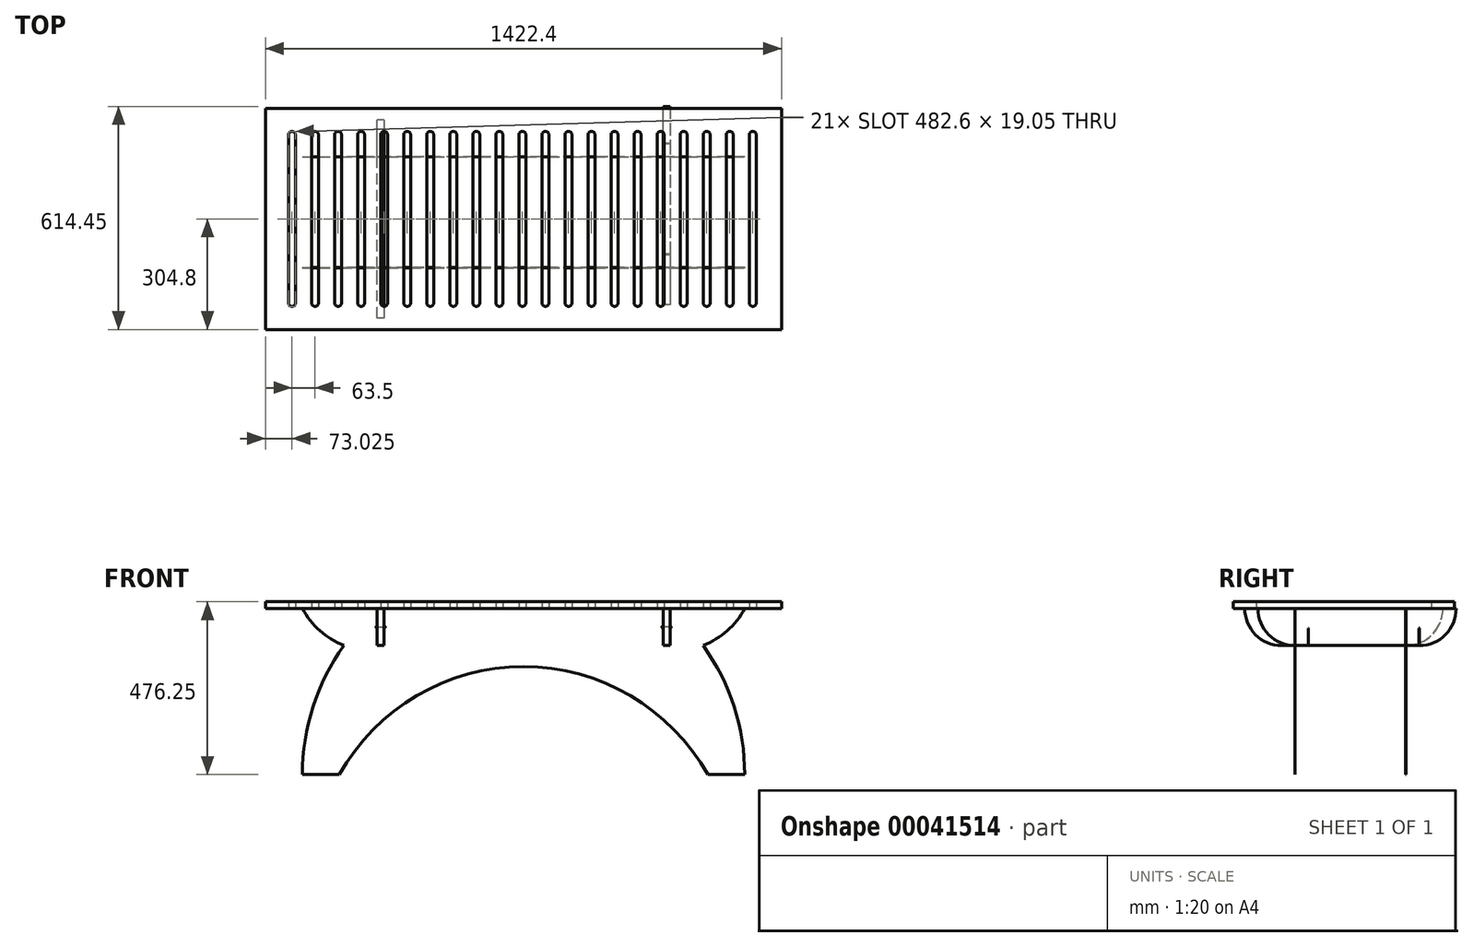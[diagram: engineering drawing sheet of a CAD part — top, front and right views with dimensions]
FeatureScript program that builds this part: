
annotation { "Feature Type Name" : "Feature", "Feature Type Description" : "" }
export const myFeature = defineFeature(function(context is Context, id is Id, definition is map)
    precondition{}
    {
        {
            assignVariable(context, id + "F0", {"name" : "Thickness", "anyValue" : .75});
        }
        {
            var Q0;
            Q0=qCreatedBy(makeId("Front.planeOp"),FACE);
            var sketch = newSketch(context, id + "F1", { "sketchPlane" : qUnion([Q0])});
            skLineSegment(sketch, "E0.bottom", {"start": v(-305.21, 223.52) * mm, "end": v(-99.17, 223.52) * mm});
            skLineSegment(sketch, "E0.top", {"start": v(-305.21, -233.68) * mm, "end": v(-203.61, -233.68) * mm});
            skLineSegment(sketch, "E1", {"start": v(913.99, -233.68) * mm, "end": v(812.39, -233.68) * mm});
            skArc(sketch, "E2", {"start": v(812.39, -233.68) * mm, "mid": v(304.39, 63.53) * mm, "end": v(-203.61, -233.68) * mm});
            skArc(sketch, "E3", {"start": v(913.99, -233.68) * mm, "mid": v(884.67, -46.9) * mm, "end": v(799.53, 121.92) * mm});
            skArc(sketch, "E4.trimOffspring", {"start": v(-190.75, 121.92) * mm, "mid": v(-275.89, -46.9) * mm, "end": v(-305.21, -233.68) * mm});
            skArc(sketch, "E5", {"start": v(-305.21, 223.52) * mm, "mid": v(-256.98, 162.58) * mm, "end": v(-190.75, 121.92) * mm});
            skArc(sketch, "E6", {"start": v(799.53, 121.92) * mm, "mid": v(865.76, 162.58) * mm, "end": v(913.99, 223.52) * mm});
            skLineSegment(sketch, "E7.trimOffspring", {"start": v(812.39, -233.68) * mm, "end": v(913.99, -233.68) * mm});
            skLineSegment(sketch, "E8", {"start": v(-99.17, 223.52) * mm, "end": v(-99.17, 175.9) * mm});
            skLineSegment(sketch, "E9", {"start": v(-96, 172.72) * mm, "end": v(-83.3, 172.72) * mm});
            skLineSegment(sketch, "E10", {"start": v(-80.12, 175.9) * mm, "end": v(-80.12, 223.52) * mm});
            skLineSegment(sketch, "E11", {"start": v(304.39, 63.53) * mm, "end": v(304.39, 223.52) * mm, "construction": true});
            skLineSegment(sketch, "E12.MirrorCS", {"start": v(707.95, 223.52) * mm, "end": v(707.95, 175.9) * mm});
            skLineSegment(sketch, "E13.MirrorCS", {"start": v(688.9, 175.9) * mm, "end": v(688.9, 223.52) * mm});
            skLineSegment(sketch, "E14.MirrorCS", {"start": v(704.78, 172.72) * mm, "end": v(692.08, 172.72) * mm});
            skLineSegment(sketch, "E15.trimOffspring", {"start": v(-80.12, 223.52) * mm, "end": v(688.9, 223.52) * mm});
            skLineSegment(sketch, "E16.trimOffspring", {"start": v(707.95, 223.52) * mm, "end": v(913.99, 223.52) * mm});
            skArc(sketch, "E17", {"start": v(-99.17, 175.9) * mm, "mid": v(-101.42, 170.48) * mm, "end": v(-96, 172.72) * mm});
            skArc(sketch, "E18", {"start": v(-83.3, 172.72) * mm, "mid": v(-77.88, 170.48) * mm, "end": v(-80.12, 175.9) * mm});
            skArc(sketch, "E19", {"start": v(688.9, 175.9) * mm, "mid": v(686.66, 170.48) * mm, "end": v(692.08, 172.72) * mm});
            skArc(sketch, "E20", {"start": v(704.78, 172.72) * mm, "mid": v(710.2, 170.48) * mm, "end": v(707.95, 175.9) * mm});
            skSolve(sketch);
        }
        {
            var Q0;
            Q0=qSketchRegion(id+"F1",true);
            extrude(context, id + "F2", {"entities" : qUnion([Q0]), "depth" : (getVariable(context, 'Thickness')) * mm});
        }
        {
            var Q0;
            Q0=makeQuery(id+"F2.opExtrude","CAP_FACE",FACE,{"disambiguationData":[OSD([sQuery(id+"F1.wireOp",EDGE,"E0.bottom"),sQuery(id+"F1.wireOp",EDGE,"E0.top"),sQuery(id+"F1.wireOp",EDGE,"E2"),sQuery(id+"F1.wireOp",EDGE,"E3"),sQuery(id+"F1.wireOp",EDGE,"E4.trimOffspring"),sQuery(id+"F1.wireOp",EDGE,"E5"),sQuery(id+"F1.wireOp",EDGE,"E6"),sQuery(id+"F1.wireOp",EDGE,"E7.trimOffspring"),sQuery(id+"F1.wireOp",EDGE,"E8"),sQuery(id+"F1.wireOp",EDGE,"E9"),sQuery(id+"F1.wireOp",EDGE,"E10"),sQuery(id+"F1.wireOp",EDGE,"E12.MirrorCS"),sQuery(id+"F1.wireOp",EDGE,"E13.MirrorCS"),sQuery(id+"F1.wireOp",EDGE,"E14.MirrorCS"),sQuery(id+"F1.wireOp",EDGE,"E15.trimOffspring"),sQuery(id+"F1.wireOp",EDGE,"E16.trimOffspring")])],"isStart":false});
            cPlane(context, id + "F3", {"entities" : qUnion([Q0]), "cplaneType" : CPlaneType.OFFSET, "offset" : 152.4 * mm, "width" : 152.4 * mm, "height" : 152.4 * mm});
        }
        {
            var Q0;
            Q0=makeQuery(id+"F2.opExtrude","SWEPT_BODY",BODY,{"disambiguationData":[OSD([sQuery(id+"F1.wireOp",EDGE,"E0.bottom"),sQuery(id+"F1.wireOp",EDGE,"E0.top"),sQuery(id+"F1.wireOp",EDGE,"E2"),sQuery(id+"F1.wireOp",EDGE,"E3"),sQuery(id+"F1.wireOp",EDGE,"E4.trimOffspring"),sQuery(id+"F1.wireOp",EDGE,"E5"),sQuery(id+"F1.wireOp",EDGE,"E6"),sQuery(id+"F1.wireOp",EDGE,"E7.trimOffspring"),sQuery(id+"F1.wireOp",EDGE,"E8"),sQuery(id+"F1.wireOp",EDGE,"E9"),sQuery(id+"F1.wireOp",EDGE,"E10"),sQuery(id+"F1.wireOp",EDGE,"E12.MirrorCS"),sQuery(id+"F1.wireOp",EDGE,"E13.MirrorCS"),sQuery(id+"F1.wireOp",EDGE,"E14.MirrorCS"),sQuery(id+"F1.wireOp",EDGE,"E15.trimOffspring"),sQuery(id+"F1.wireOp",EDGE,"E16.trimOffspring")])]});
            var Q1;
            Q1=qCreatedBy(id+"F3.planeOp",FACE);
            mirror(context, id + "F4", {"entities" : qUnion([Q0]), "mirrorPlane" : qUnion([Q1])});
        }
        {
            var Q0;
            Q0=makeQuery(id+"F4.opPattern","COPY",FACE,{"derivedFrom":makeQuery(id+"F2.opExtrude","SWEPT_FACE",FACE,{"disambiguationData":[OSD([sQuery(id+"F1.wireOp",EDGE,"E8")])]}),"instanceName":"1"});
            var sketch = newSketch(context, id + "F5", { "sketchPlane" : qUnion([Q0])});
            skLineSegment(sketch, "E21.bottom", {"start": v(-444.5, 223.52) * mm, "end": v(101.6, 223.52) * mm});
            skLineSegment(sketch, "E21.top", {"start": v(-342.9, 121.92) * mm, "end": v(0, 121.92) * mm});
            skArc(sketch, "E22", {"start": v(-444.5, 223.52) * mm, "mid": v(-414.74, 151.68) * mm, "end": v(-342.9, 121.92) * mm});
            skArc(sketch, "E23.converted", {"start": v(0, 121.92) * mm, "mid": v(71.84, 151.68) * mm, "end": v(101.6, 223.52) * mm});
            skSolve(sketch);
        }
        {
            var Q0;
            Q0=qSketchRegion(id+"F5",true);
            var Q1;
            Q1=makeQuery(id+"F2.opExtrude","SWEPT_FACE",FACE,{"disambiguationData":[OSD([sQuery(id+"F1.wireOp",EDGE,"E10")])]});
            extrude(context, id + "F6", {"entities" : qUnion([Q0]), "endBound" : BoundingType.UP_TO_SURFACE, "endBoundEntityFace" : qUnion([Q1]), "depth" : 25.4 * mm});
        }
        {
            var Q0;
            Q0=makeQuery(id+"F2.opExtrude","SWEPT_BODY",BODY,{"disambiguationData":[OSD([sQuery(id+"F1.wireOp",EDGE,"E0.bottom"),sQuery(id+"F1.wireOp",EDGE,"E0.top"),sQuery(id+"F1.wireOp",EDGE,"E2"),sQuery(id+"F1.wireOp",EDGE,"E3"),sQuery(id+"F1.wireOp",EDGE,"E4.trimOffspring"),sQuery(id+"F1.wireOp",EDGE,"E5"),sQuery(id+"F1.wireOp",EDGE,"E6"),sQuery(id+"F1.wireOp",EDGE,"E7.trimOffspring"),sQuery(id+"F1.wireOp",EDGE,"E8"),sQuery(id+"F1.wireOp",EDGE,"E9"),sQuery(id+"F1.wireOp",EDGE,"E10"),sQuery(id+"F1.wireOp",EDGE,"E12.MirrorCS"),sQuery(id+"F1.wireOp",EDGE,"E13.MirrorCS"),sQuery(id+"F1.wireOp",EDGE,"E14.MirrorCS"),sQuery(id+"F1.wireOp",EDGE,"E15.trimOffspring"),sQuery(id+"F1.wireOp",EDGE,"E16.trimOffspring")])]});
            var Q1;
            Q1=makeQuery(id+"F4.opPattern","COPY",BODY,{"derivedFrom":makeQuery(id+"F2.opExtrude","SWEPT_BODY",BODY,{"disambiguationData":[OSD([sQuery(id+"F1.wireOp",EDGE,"E0.bottom"),sQuery(id+"F1.wireOp",EDGE,"E0.top"),sQuery(id+"F1.wireOp",EDGE,"E2"),sQuery(id+"F1.wireOp",EDGE,"E3"),sQuery(id+"F1.wireOp",EDGE,"E4.trimOffspring"),sQuery(id+"F1.wireOp",EDGE,"E5"),sQuery(id+"F1.wireOp",EDGE,"E6"),sQuery(id+"F1.wireOp",EDGE,"E7.trimOffspring"),sQuery(id+"F1.wireOp",EDGE,"E8"),sQuery(id+"F1.wireOp",EDGE,"E9"),sQuery(id+"F1.wireOp",EDGE,"E10"),sQuery(id+"F1.wireOp",EDGE,"E12.MirrorCS"),sQuery(id+"F1.wireOp",EDGE,"E13.MirrorCS"),sQuery(id+"F1.wireOp",EDGE,"E14.MirrorCS"),sQuery(id+"F1.wireOp",EDGE,"E15.trimOffspring"),sQuery(id+"F1.wireOp",EDGE,"E16.trimOffspring")])]}),"instanceName":"1"});
            var Q2;
            Q2=makeQuery(id+"F6.opExtrude","SWEPT_BODY",BODY,{"disambiguationData":[OSD([sQuery(id+"F5.wireOp",EDGE,"E21.bottom"),sQuery(id+"F5.wireOp",EDGE,"E21.top"),sQuery(id+"F5.wireOp",EDGE,"E22"),sQuery(id+"F5.wireOp",EDGE,"E23.converted")])]});
            booleanBodies(context, id + "F7", {"operationType" : BooleanOperationType.SUBTRACTION, "tools" : qUnion([Q0, Q1]), "targets" : qUnion([Q2]), "keepTools" : true});
        }
        {
            var Q0;
            Q0=makeQuery(id+"F2.opExtrude","SWEPT_FACE",FACE,{"disambiguationData":[OSD([sQuery(id+"F1.wireOp",EDGE,"E12.MirrorCS")])]});
            var Q1;
            Q1=makeQuery(id+"F6.opExtrude","CAP_FACE",FACE,{"disambiguationData":[OSD([sQuery(id+"F5.wireOp",EDGE,"E21.bottom"),sQuery(id+"F5.wireOp",EDGE,"E21.top"),sQuery(id+"F5.wireOp",EDGE,"E22"),sQuery(id+"F5.wireOp",EDGE,"E23.converted")])],"isStart":true});
            cPlane(context, id + "F8", {"entities" : qUnion([Q0, Q1]), "cplaneType" : CPlaneType.MID_PLANE, "offset" : 152.4 * mm, "width" : 152.4 * mm, "height" : 152.4 * mm});
        }
        {
            var Q0;
            Q0=makeQuery(id+"F6.opExtrude","SWEPT_BODY",BODY,{"disambiguationData":[OSD([sQuery(id+"F5.wireOp",EDGE,"E21.bottom"),sQuery(id+"F5.wireOp",EDGE,"E21.top"),sQuery(id+"F5.wireOp",EDGE,"E22"),sQuery(id+"F5.wireOp",EDGE,"E23.converted")])]});
            var Q1;
            Q1=sQuery(id+"F5.wireOp",VERTEX,"E22.center");
            var Q2;
            Q2=makeQuery(id+"F4.opPattern","COPY",VERTEX,{"derivedFrom":makeQuery(id+"F2.opExtrude","CAP_VERTEX",VERTEX,{"disambiguationData":[OSD([sQuery(id+"F1.wireOp",EDGE,"E13.MirrorCS"),sQuery(id+"F1.wireOp",EDGE,"E15.trimOffspring")])],"isStart":true}),"instanceName":"1"});
            transform(context, id + "F9", {"entities" : qUnion([Q0]), "transformType" : TransformType.TRANSLATION_ENTITY, "oppositeDirectionEntity" : false, "transformLine" : qUnion([Q1, Q2]), "makeCopy" : true});
        }
        {
            var Q0;
            Q0=qCreatedBy(makeId("Top.planeOp"),FACE);
            var sketch = newSketch(context, id + "F10", { "sketchPlane" : qUnion([Q0])});
            skLineSegment(sketch, "E24.bottom", {"start": v(-252.18, 107.3) * mm, "end": v(1170.22, 107.3) * mm});
            skLineSegment(sketch, "E24.top", {"start": v(-252.18, -502.3) * mm, "end": v(1170.22, -502.3) * mm});
            skLineSegment(sketch, "E24.left", {"start": v(-252.18, 107.3) * mm, "end": v(-252.18, -502.3) * mm});
            skLineSegment(sketch, "E24.right", {"start": v(1170.22, 107.3) * mm, "end": v(1170.22, -502.3) * mm});
            skLineSegment(sketch, "E25.bottom", {"start": v(-179.15, 43.8) * mm, "end": v(-179.15, 43.8) * mm});
            skLineSegment(sketch, "E25.top", {"start": v(-179.15, -438.8) * mm, "end": v(-179.15, -438.8) * mm});
            skLineSegment(sketch, "E25.left", {"start": v(-188.68, 34.27) * mm, "end": v(-188.68, -429.28) * mm});
            skLineSegment(sketch, "E25.right", {"start": v(-169.63, 34.27) * mm, "end": v(-169.63, -429.28) * mm});
            skPoint(sketch, "E26.visualSharp", {"position": v(-188.68, 43.8) * mm});
            skArc(sketch, "E26.filletArc", {"start": v(-179.15, 43.8) * mm, "mid": v(-185.89, 41) * mm, "end": v(-188.68, 34.27) * mm});
            skPoint(sketch, "E27.visualSharp", {"position": v(-169.63, 43.8) * mm});
            skArc(sketch, "E27.filletArc", {"start": v(-169.63, 34.27) * mm, "mid": v(-172.42, 41) * mm, "end": v(-179.15, 43.8) * mm});
            skPoint(sketch, "E28.visualSharp", {"position": v(-188.68, -438.8) * mm});
            skArc(sketch, "E28.filletArc", {"start": v(-188.68, -429.28) * mm, "mid": v(-185.89, -436.01) * mm, "end": v(-179.15, -438.8) * mm});
            skPoint(sketch, "E29.visualSharp", {"position": v(-169.63, -438.8) * mm});
            skArc(sketch, "E29.filletArc", {"start": v(-179.15, -438.8) * mm, "mid": v(-172.42, -436.01) * mm, "end": v(-169.63, -429.28) * mm});
            skArc(sketch, "E30.1.0.0", {"start": v(-115.65, 43.8) * mm, "mid": v(-122.39, 41) * mm, "end": v(-125.18, 34.27) * mm});
            skArc(sketch, "E30.1.0.1", {"start": v(-106.13, 34.27) * mm, "mid": v(-108.92, 41) * mm, "end": v(-115.65, 43.8) * mm});
            skLineSegment(sketch, "E30.1.0.2", {"start": v(-106.13, 34.27) * mm, "end": v(-106.13, -429.28) * mm});
            skLineSegment(sketch, "E30.1.0.3", {"start": v(-125.18, 34.27) * mm, "end": v(-125.18, -429.28) * mm});
            skArc(sketch, "E30.1.0.4", {"start": v(-125.18, -429.28) * mm, "mid": v(-122.39, -436.01) * mm, "end": v(-115.65, -438.8) * mm});
            skArc(sketch, "E30.1.0.5", {"start": v(-115.65, -438.8) * mm, "mid": v(-108.92, -436.01) * mm, "end": v(-106.13, -429.28) * mm});
            skArc(sketch, "E30.2.0.0", {"start": v(-52.15, 43.8) * mm, "mid": v(-58.89, 41) * mm, "end": v(-61.68, 34.27) * mm});
            skArc(sketch, "E30.2.0.1", {"start": v(-42.63, 34.27) * mm, "mid": v(-45.42, 41) * mm, "end": v(-52.15, 43.8) * mm});
            skLineSegment(sketch, "E30.2.0.2", {"start": v(-42.63, 34.27) * mm, "end": v(-42.63, -429.28) * mm});
            skLineSegment(sketch, "E30.2.0.3", {"start": v(-61.68, 34.27) * mm, "end": v(-61.68, -429.28) * mm});
            skArc(sketch, "E30.2.0.4", {"start": v(-61.68, -429.28) * mm, "mid": v(-58.89, -436.01) * mm, "end": v(-52.15, -438.8) * mm});
            skArc(sketch, "E30.2.0.5", {"start": v(-52.15, -438.8) * mm, "mid": v(-45.42, -436.01) * mm, "end": v(-42.63, -429.28) * mm});
            skArc(sketch, "E30.3.0.0", {"start": v(11.35, 43.8) * mm, "mid": v(4.61, 41) * mm, "end": v(1.82, 34.27) * mm});
            skArc(sketch, "E30.3.0.1", {"start": v(20.87, 34.27) * mm, "mid": v(18.08, 41) * mm, "end": v(11.35, 43.8) * mm});
            skLineSegment(sketch, "E30.3.0.2", {"start": v(20.87, 34.27) * mm, "end": v(20.87, -429.28) * mm});
            skLineSegment(sketch, "E30.3.0.3", {"start": v(1.82, 34.27) * mm, "end": v(1.82, -429.28) * mm});
            skArc(sketch, "E30.3.0.4", {"start": v(1.82, -429.28) * mm, "mid": v(4.61, -436.01) * mm, "end": v(11.35, -438.8) * mm});
            skArc(sketch, "E30.3.0.5", {"start": v(11.35, -438.8) * mm, "mid": v(18.08, -436.01) * mm, "end": v(20.87, -429.28) * mm});
            skArc(sketch, "E30.4.0.0", {"start": v(74.85, 43.8) * mm, "mid": v(68.11, 41) * mm, "end": v(65.32, 34.27) * mm});
            skArc(sketch, "E30.4.0.1", {"start": v(84.37, 34.27) * mm, "mid": v(81.58, 41) * mm, "end": v(74.85, 43.8) * mm});
            skLineSegment(sketch, "E30.4.0.2", {"start": v(84.37, 34.27) * mm, "end": v(84.37, -429.28) * mm});
            skLineSegment(sketch, "E30.4.0.3", {"start": v(65.32, 34.27) * mm, "end": v(65.32, -429.28) * mm});
            skArc(sketch, "E30.4.0.4", {"start": v(65.32, -429.28) * mm, "mid": v(68.11, -436.01) * mm, "end": v(74.85, -438.8) * mm});
            skArc(sketch, "E30.4.0.5", {"start": v(74.85, -438.8) * mm, "mid": v(81.58, -436.01) * mm, "end": v(84.37, -429.28) * mm});
            skArc(sketch, "E30.5.0.0", {"start": v(138.35, 43.8) * mm, "mid": v(131.61, 41) * mm, "end": v(128.82, 34.27) * mm});
            skArc(sketch, "E30.5.0.1", {"start": v(147.87, 34.27) * mm, "mid": v(145.08, 41) * mm, "end": v(138.35, 43.8) * mm});
            skLineSegment(sketch, "E30.5.0.2", {"start": v(147.87, 34.27) * mm, "end": v(147.87, -429.28) * mm});
            skLineSegment(sketch, "E30.5.0.3", {"start": v(128.82, 34.27) * mm, "end": v(128.82, -429.28) * mm});
            skArc(sketch, "E30.5.0.4", {"start": v(128.82, -429.28) * mm, "mid": v(131.61, -436.01) * mm, "end": v(138.35, -438.8) * mm});
            skArc(sketch, "E30.5.0.5", {"start": v(138.35, -438.8) * mm, "mid": v(145.08, -436.01) * mm, "end": v(147.87, -429.28) * mm});
            skArc(sketch, "E30.6.0.0", {"start": v(201.85, 43.8) * mm, "mid": v(195.11, 41) * mm, "end": v(192.32, 34.27) * mm});
            skArc(sketch, "E30.6.0.1", {"start": v(211.37, 34.27) * mm, "mid": v(208.58, 41) * mm, "end": v(201.85, 43.8) * mm});
            skLineSegment(sketch, "E30.6.0.2", {"start": v(211.37, 34.27) * mm, "end": v(211.37, -429.28) * mm});
            skLineSegment(sketch, "E30.6.0.3", {"start": v(192.32, 34.27) * mm, "end": v(192.32, -429.28) * mm});
            skArc(sketch, "E30.6.0.4", {"start": v(192.32, -429.28) * mm, "mid": v(195.11, -436.01) * mm, "end": v(201.85, -438.8) * mm});
            skArc(sketch, "E30.6.0.5", {"start": v(201.85, -438.8) * mm, "mid": v(208.58, -436.01) * mm, "end": v(211.37, -429.28) * mm});
            skArc(sketch, "E30.7.0.0", {"start": v(265.35, 43.8) * mm, "mid": v(258.61, 41) * mm, "end": v(255.82, 34.27) * mm});
            skArc(sketch, "E30.7.0.1", {"start": v(274.87, 34.27) * mm, "mid": v(272.08, 41) * mm, "end": v(265.35, 43.8) * mm});
            skLineSegment(sketch, "E30.7.0.2", {"start": v(274.87, 34.27) * mm, "end": v(274.87, -429.28) * mm});
            skLineSegment(sketch, "E30.7.0.3", {"start": v(255.82, 34.27) * mm, "end": v(255.82, -429.28) * mm});
            skArc(sketch, "E30.7.0.4", {"start": v(255.82, -429.28) * mm, "mid": v(258.61, -436.01) * mm, "end": v(265.35, -438.8) * mm});
            skArc(sketch, "E30.7.0.5", {"start": v(265.35, -438.8) * mm, "mid": v(272.08, -436.01) * mm, "end": v(274.87, -429.28) * mm});
            skArc(sketch, "E30.8.0.0", {"start": v(328.85, 43.8) * mm, "mid": v(322.11, 41) * mm, "end": v(319.32, 34.27) * mm});
            skArc(sketch, "E30.8.0.1", {"start": v(338.37, 34.27) * mm, "mid": v(335.58, 41) * mm, "end": v(328.85, 43.8) * mm});
            skLineSegment(sketch, "E30.8.0.2", {"start": v(338.37, 34.27) * mm, "end": v(338.37, -429.28) * mm});
            skLineSegment(sketch, "E30.8.0.3", {"start": v(319.32, 34.27) * mm, "end": v(319.32, -429.28) * mm});
            skArc(sketch, "E30.8.0.4", {"start": v(319.32, -429.28) * mm, "mid": v(322.11, -436.01) * mm, "end": v(328.85, -438.8) * mm});
            skArc(sketch, "E30.8.0.5", {"start": v(328.85, -438.8) * mm, "mid": v(335.58, -436.01) * mm, "end": v(338.37, -429.28) * mm});
            skArc(sketch, "E30.9.0.0", {"start": v(392.35, 43.8) * mm, "mid": v(385.61, 41) * mm, "end": v(382.82, 34.27) * mm});
            skArc(sketch, "E30.9.0.1", {"start": v(401.87, 34.27) * mm, "mid": v(399.08, 41) * mm, "end": v(392.35, 43.8) * mm});
            skLineSegment(sketch, "E30.9.0.2", {"start": v(401.87, 34.27) * mm, "end": v(401.87, -429.28) * mm});
            skLineSegment(sketch, "E30.9.0.3", {"start": v(382.82, 34.27) * mm, "end": v(382.82, -429.28) * mm});
            skArc(sketch, "E30.9.0.4", {"start": v(382.82, -429.28) * mm, "mid": v(385.61, -436.01) * mm, "end": v(392.35, -438.8) * mm});
            skArc(sketch, "E30.9.0.5", {"start": v(392.35, -438.8) * mm, "mid": v(399.08, -436.01) * mm, "end": v(401.87, -429.28) * mm});
            skArc(sketch, "E30.10.0.0", {"start": v(455.85, 43.8) * mm, "mid": v(449.11, 41) * mm, "end": v(446.32, 34.27) * mm});
            skArc(sketch, "E30.10.0.1", {"start": v(465.37, 34.27) * mm, "mid": v(462.58, 41) * mm, "end": v(455.85, 43.8) * mm});
            skLineSegment(sketch, "E30.10.0.2", {"start": v(465.37, 34.27) * mm, "end": v(465.37, -429.28) * mm});
            skLineSegment(sketch, "E30.10.0.3", {"start": v(446.32, 34.27) * mm, "end": v(446.32, -429.28) * mm});
            skArc(sketch, "E30.10.0.4", {"start": v(446.32, -429.28) * mm, "mid": v(449.11, -436.01) * mm, "end": v(455.85, -438.8) * mm});
            skArc(sketch, "E30.10.0.5", {"start": v(455.85, -438.8) * mm, "mid": v(462.58, -436.01) * mm, "end": v(465.37, -429.28) * mm});
            skArc(sketch, "E30.11.0.0", {"start": v(519.35, 43.8) * mm, "mid": v(512.61, 41) * mm, "end": v(509.82, 34.27) * mm});
            skArc(sketch, "E30.11.0.1", {"start": v(528.87, 34.27) * mm, "mid": v(526.08, 41) * mm, "end": v(519.35, 43.8) * mm});
            skLineSegment(sketch, "E30.11.0.2", {"start": v(528.87, 34.27) * mm, "end": v(528.87, -429.28) * mm});
            skLineSegment(sketch, "E30.11.0.3", {"start": v(509.82, 34.27) * mm, "end": v(509.82, -429.28) * mm});
            skArc(sketch, "E30.11.0.4", {"start": v(509.82, -429.28) * mm, "mid": v(512.61, -436.01) * mm, "end": v(519.35, -438.8) * mm});
            skArc(sketch, "E30.11.0.5", {"start": v(519.35, -438.8) * mm, "mid": v(526.08, -436.01) * mm, "end": v(528.87, -429.28) * mm});
            skArc(sketch, "E30.12.0.0", {"start": v(582.85, 43.8) * mm, "mid": v(576.11, 41) * mm, "end": v(573.32, 34.27) * mm});
            skArc(sketch, "E30.12.0.1", {"start": v(592.37, 34.27) * mm, "mid": v(589.58, 41) * mm, "end": v(582.85, 43.8) * mm});
            skLineSegment(sketch, "E30.12.0.2", {"start": v(592.37, 34.27) * mm, "end": v(592.37, -429.28) * mm});
            skLineSegment(sketch, "E30.12.0.3", {"start": v(573.32, 34.27) * mm, "end": v(573.32, -429.28) * mm});
            skArc(sketch, "E30.12.0.4", {"start": v(573.32, -429.28) * mm, "mid": v(576.11, -436.01) * mm, "end": v(582.85, -438.8) * mm});
            skArc(sketch, "E30.12.0.5", {"start": v(582.85, -438.8) * mm, "mid": v(589.58, -436.01) * mm, "end": v(592.37, -429.28) * mm});
            skArc(sketch, "E30.13.0.0", {"start": v(646.35, 43.8) * mm, "mid": v(639.61, 41) * mm, "end": v(636.82, 34.27) * mm});
            skArc(sketch, "E30.13.0.1", {"start": v(655.87, 34.27) * mm, "mid": v(653.08, 41) * mm, "end": v(646.35, 43.8) * mm});
            skLineSegment(sketch, "E30.13.0.2", {"start": v(655.87, 34.27) * mm, "end": v(655.87, -429.28) * mm});
            skLineSegment(sketch, "E30.13.0.3", {"start": v(636.82, 34.27) * mm, "end": v(636.82, -429.28) * mm});
            skArc(sketch, "E30.13.0.4", {"start": v(636.82, -429.28) * mm, "mid": v(639.61, -436.01) * mm, "end": v(646.35, -438.8) * mm});
            skArc(sketch, "E30.13.0.5", {"start": v(646.35, -438.8) * mm, "mid": v(653.08, -436.01) * mm, "end": v(655.87, -429.28) * mm});
            skArc(sketch, "E30.14.0.0", {"start": v(709.85, 43.8) * mm, "mid": v(703.11, 41) * mm, "end": v(700.32, 34.27) * mm});
            skArc(sketch, "E30.14.0.1", {"start": v(719.37, 34.27) * mm, "mid": v(716.58, 41) * mm, "end": v(709.85, 43.8) * mm});
            skLineSegment(sketch, "E30.14.0.2", {"start": v(719.37, 34.27) * mm, "end": v(719.37, -429.28) * mm});
            skLineSegment(sketch, "E30.14.0.3", {"start": v(700.32, 34.27) * mm, "end": v(700.32, -429.28) * mm});
            skArc(sketch, "E30.14.0.4", {"start": v(700.32, -429.28) * mm, "mid": v(703.11, -436.01) * mm, "end": v(709.85, -438.8) * mm});
            skArc(sketch, "E30.14.0.5", {"start": v(709.85, -438.8) * mm, "mid": v(716.58, -436.01) * mm, "end": v(719.37, -429.28) * mm});
            skArc(sketch, "E30.15.0.0", {"start": v(773.35, 43.8) * mm, "mid": v(766.61, 41) * mm, "end": v(763.82, 34.27) * mm});
            skArc(sketch, "E30.15.0.1", {"start": v(782.87, 34.27) * mm, "mid": v(780.08, 41) * mm, "end": v(773.35, 43.8) * mm});
            skLineSegment(sketch, "E30.15.0.2", {"start": v(782.87, 34.27) * mm, "end": v(782.87, -429.28) * mm});
            skLineSegment(sketch, "E30.15.0.3", {"start": v(763.82, 34.27) * mm, "end": v(763.82, -429.28) * mm});
            skArc(sketch, "E30.15.0.4", {"start": v(763.82, -429.28) * mm, "mid": v(766.61, -436.01) * mm, "end": v(773.35, -438.8) * mm});
            skArc(sketch, "E30.15.0.5", {"start": v(773.35, -438.8) * mm, "mid": v(780.08, -436.01) * mm, "end": v(782.87, -429.28) * mm});
            skArc(sketch, "E30.16.0.0", {"start": v(836.85, 43.8) * mm, "mid": v(830.11, 41) * mm, "end": v(827.32, 34.27) * mm});
            skArc(sketch, "E30.16.0.1", {"start": v(846.37, 34.27) * mm, "mid": v(843.58, 41) * mm, "end": v(836.85, 43.8) * mm});
            skLineSegment(sketch, "E30.16.0.2", {"start": v(846.37, 34.27) * mm, "end": v(846.37, -429.28) * mm});
            skLineSegment(sketch, "E30.16.0.3", {"start": v(827.32, 34.27) * mm, "end": v(827.32, -429.28) * mm});
            skArc(sketch, "E30.16.0.4", {"start": v(827.32, -429.28) * mm, "mid": v(830.11, -436.01) * mm, "end": v(836.85, -438.8) * mm});
            skArc(sketch, "E30.16.0.5", {"start": v(836.85, -438.8) * mm, "mid": v(843.58, -436.01) * mm, "end": v(846.37, -429.28) * mm});
            skArc(sketch, "E30.17.0.0", {"start": v(900.35, 43.8) * mm, "mid": v(893.61, 41) * mm, "end": v(890.82, 34.27) * mm});
            skArc(sketch, "E30.17.0.1", {"start": v(909.87, 34.27) * mm, "mid": v(907.08, 41) * mm, "end": v(900.35, 43.8) * mm});
            skLineSegment(sketch, "E30.17.0.2", {"start": v(909.87, 34.27) * mm, "end": v(909.87, -429.28) * mm});
            skLineSegment(sketch, "E30.17.0.3", {"start": v(890.82, 34.27) * mm, "end": v(890.82, -429.28) * mm});
            skArc(sketch, "E30.17.0.4", {"start": v(890.82, -429.28) * mm, "mid": v(893.61, -436.01) * mm, "end": v(900.35, -438.8) * mm});
            skArc(sketch, "E30.17.0.5", {"start": v(900.35, -438.8) * mm, "mid": v(907.08, -436.01) * mm, "end": v(909.87, -429.28) * mm});
            skArc(sketch, "E30.18.0.0", {"start": v(963.85, 43.8) * mm, "mid": v(957.11, 41) * mm, "end": v(954.32, 34.27) * mm});
            skArc(sketch, "E30.18.0.1", {"start": v(973.37, 34.27) * mm, "mid": v(970.58, 41) * mm, "end": v(963.85, 43.8) * mm});
            skLineSegment(sketch, "E30.18.0.2", {"start": v(973.37, 34.27) * mm, "end": v(973.37, -429.28) * mm});
            skLineSegment(sketch, "E30.18.0.3", {"start": v(954.32, 34.27) * mm, "end": v(954.32, -429.28) * mm});
            skArc(sketch, "E30.18.0.4", {"start": v(954.32, -429.28) * mm, "mid": v(957.11, -436.01) * mm, "end": v(963.85, -438.8) * mm});
            skArc(sketch, "E30.18.0.5", {"start": v(963.85, -438.8) * mm, "mid": v(970.58, -436.01) * mm, "end": v(973.37, -429.28) * mm});
            skArc(sketch, "E30.19.0.0", {"start": v(1027.35, 43.8) * mm, "mid": v(1020.61, 41) * mm, "end": v(1017.82, 34.27) * mm});
            skArc(sketch, "E30.19.0.1", {"start": v(1036.87, 34.27) * mm, "mid": v(1034.08, 41) * mm, "end": v(1027.35, 43.8) * mm});
            skLineSegment(sketch, "E30.19.0.2", {"start": v(1036.87, 34.27) * mm, "end": v(1036.87, -429.28) * mm});
            skLineSegment(sketch, "E30.19.0.3", {"start": v(1017.82, 34.27) * mm, "end": v(1017.82, -429.28) * mm});
            skArc(sketch, "E30.19.0.4", {"start": v(1017.82, -429.28) * mm, "mid": v(1020.61, -436.01) * mm, "end": v(1027.35, -438.8) * mm});
            skArc(sketch, "E30.19.0.5", {"start": v(1027.35, -438.8) * mm, "mid": v(1034.08, -436.01) * mm, "end": v(1036.87, -429.28) * mm});
            skArc(sketch, "E30.20.0.0", {"start": v(1090.85, 43.8) * mm, "mid": v(1084.11, 41) * mm, "end": v(1081.32, 34.27) * mm});
            skArc(sketch, "E30.20.0.1", {"start": v(1100.37, 34.27) * mm, "mid": v(1097.58, 41) * mm, "end": v(1090.85, 43.8) * mm});
            skLineSegment(sketch, "E30.20.0.2", {"start": v(1100.37, 34.27) * mm, "end": v(1100.37, -429.28) * mm});
            skLineSegment(sketch, "E30.20.0.3", {"start": v(1081.32, 34.27) * mm, "end": v(1081.32, -429.28) * mm});
            skArc(sketch, "E30.20.0.4", {"start": v(1081.32, -429.28) * mm, "mid": v(1084.11, -436.01) * mm, "end": v(1090.85, -438.8) * mm});
            skArc(sketch, "E30.20.0.5", {"start": v(1090.85, -438.8) * mm, "mid": v(1097.58, -436.01) * mm, "end": v(1100.37, -429.28) * mm});
            skLineSegment(sketch, "E30.direction1", {"start": v(-188.68, 34.27) * mm, "end": v(-125.18, 34.27) * mm, "construction": true});
            skSolve(sketch);
        }
        {
            var Q0;
            Q0=qSketchRegion(id+"F10",true);
            extrude(context, id + "F11", {"entities" : qUnion([Q0]), "depth" : 19.05 * mm});
        }
        {
            var Q0;
            Q0=makeQuery(id+"F2.opExtrude","SWEPT_FACE",FACE,{"disambiguationData":[OSD([sQuery(id+"F1.wireOp",EDGE,"E0.bottom")])]});
            var sketch = newSketch(context, id + "F12", { "sketchPlane" : qUnion([Q0])});
            skLineSegment(sketch, "E31", {"start": v(-305.21, 0) * mm, "end": v(-305.21, 133.35) * mm});
            skLineSegment(sketch, "E32", {"start": v(-305.21, 133.35) * mm, "end": v(-406.81, 133.35) * mm});
            skSolve(sketch);
        }
        {
            var Q0;
            Q0=makeQuery(id+"F11.opExtrude","SWEPT_BODY",BODY,{"disambiguationData":[OSD([sQuery(id+"F10.wireOp",EDGE,"E24.bottom"),sQuery(id+"F10.wireOp",EDGE,"E24.top"),sQuery(id+"F10.wireOp",EDGE,"E24.left"),sQuery(id+"F10.wireOp",EDGE,"E24.right")])]});
            var Q1;
            Q1=sQuery(id+"F12.wireOp",VERTEX,"E32.end");
            var Q2;
            Q2=makeQuery(id+"F11.opExtrude","CAP_VERTEX",VERTEX,{"disambiguationData":[OSD([sQuery(id+"F10.wireOp",EDGE,"E24.bottom"),sQuery(id+"F10.wireOp",EDGE,"E24.left")])],"isStart":true});
            transform(context, id + "F13", {"entities" : qUnion([Q0]), "transformType" : TransformType.TRANSLATION_ENTITY, "oppositeDirectionEntity" : true, "transformLine" : qUnion([Q1, Q2]), "makeCopy" : false});
        }
    });
